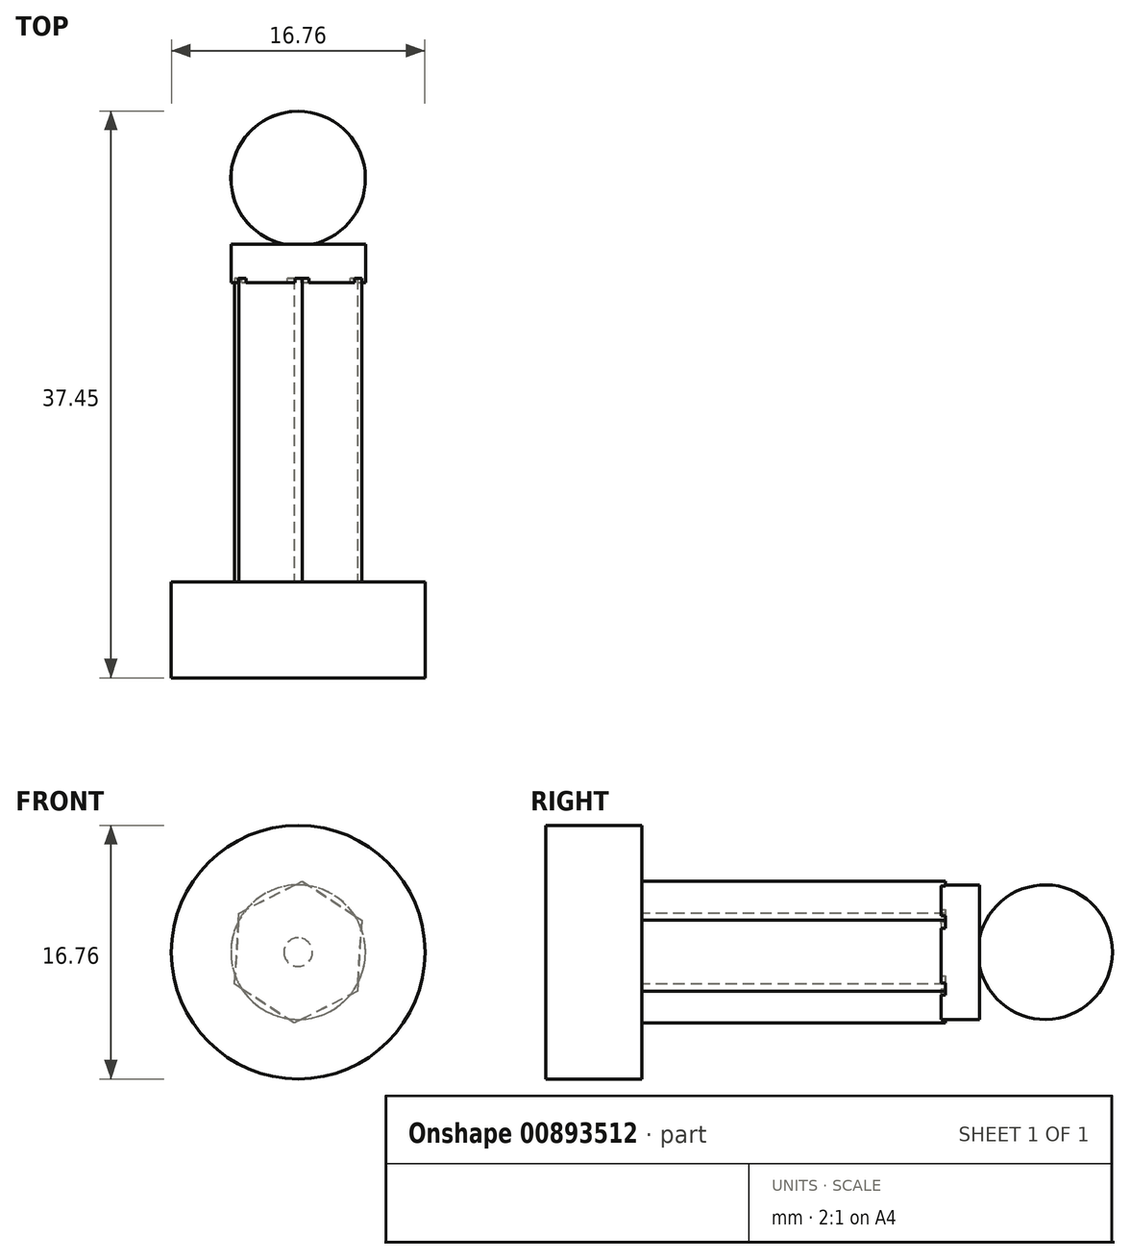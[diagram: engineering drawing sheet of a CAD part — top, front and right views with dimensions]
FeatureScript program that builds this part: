
annotation { "Feature Type Name" : "Feature", "Feature Type Description" : "" }
export const myFeature = defineFeature(function(context is Context, id is Id, definition is map)
    precondition{}
    {
        {
            var Q0;
            Q0=qCreatedBy(makeId("Top.planeOp"),FACE);
            var sketch = newSketch(context, id + "F0", { "sketchPlane" : qUnion([Q0])});
            skArc(sketch, "E0", {"start": v(0, 37.45) * mm, "mid": v(-4.42, 33.48) * mm, "end": v(-0.94, 28.66) * mm});
            skLineSegment(sketch, "E1", {"start": v(0, 37.45) * mm, "end": v(0, 28.56) * mm});
            skLineSegment(sketch, "E2", {"start": v(0, 37.45) * mm, "end": v(0, 28.56) * mm, "construction": true});
            skLineSegment(sketch, "E3", {"start": v(0, 28.56) * mm, "end": v(0, 26.02) * mm, "construction": true});
            skLineSegment(sketch, "E4.bottom", {"start": v(-0.94, 28.66) * mm, "end": v(-4.45, 28.66) * mm});
            skLineSegment(sketch, "E4.top", {"start": v(0, 26.12) * mm, "end": v(-4.45, 26.12) * mm});
            skLineSegment(sketch, "E4.left", {"start": v(0, 28.66) * mm, "end": v(0, 26.12) * mm});
            skLineSegment(sketch, "E4.right", {"start": v(-4.45, 28.66) * mm, "end": v(-4.45, 26.12) * mm});
            skSolve(sketch);
        }
        {
            var Q0;
            Q0=makeQuery(id+"F0.imprint","IMPRINT",FACE,{"disambiguationData":[TD([[makeQuery(id+"F0.imprint","IMPRINT",EDGE,{"derivedFrom":sQuery(id+"F0.wireOp",EDGE,"E0")}),1.0]])]});
            var Q1;
            Q1=sQuery(id+"F0.wireOp",EDGE,"E1");
            revolve(context, id + "F1", {"surfaceOperationType" : NewSurfaceOperationType.NEW, "entities" : qUnion([Q0]), "axis" : qUnion([Q1]), "revolveType" : RevolveType.FULL});
        }
        {
            var Q0;
            Q0=qCreatedBy(makeId("Front.planeOp"),FACE);
            var sketch = newSketch(context, id + "F2", { "sketchPlane" : qUnion([Q0])});
            skCircle(sketch, "E5", {"center": v(0, 0) * mm, "radius": 8.38 * mm});
            skCircle(sketch, "E6.cCircle", {"center": v(0, 0) * mm, "radius": 4.06 * mm, "construction": true});
            skLineSegment(sketch, "E6.0", {"start": v(-0.27, -4.68) * mm, "end": v(-4.2, -2.1) * mm});
            skLineSegment(sketch, "E6.1", {"start": v(-4.2, -2.1) * mm, "end": v(-3.92, 2.58) * mm});
            skLineSegment(sketch, "E6.2", {"start": v(-3.92, 2.58) * mm, "end": v(0.27, 4.68) * mm});
            skLineSegment(sketch, "E6.3", {"start": v(0.27, 4.68) * mm, "end": v(4.2, 2.1) * mm});
            skLineSegment(sketch, "E6.4", {"start": v(4.2, 2.1) * mm, "end": v(3.92, -2.58) * mm});
            skLineSegment(sketch, "E6.5", {"start": v(3.92, -2.58) * mm, "end": v(-0.27, -4.68) * mm});
            skPoint(sketch, "E6.0.midPoint", {"position": v(-2.23, -3.4) * mm});
            skSolve(sketch);
        }
        {
            var Q0;
            Q0=makeQuery(id+"F2.imprint","IMPRINT",FACE,{"disambiguationData":[TD([[makeQuery(id+"F2.imprint","IMPRINT",EDGE,{"derivedFrom":sQuery(id+"F2.wireOp",EDGE,"E6.0")}),-1.0]])]});
            extrude(context, id + "F3", {"entities" : qUnion([Q0]), "operationType" : NewBodyOperationType.ADD, "oppositeDirection" : true, "depth" : 26.42 * mm, "offsetDistance" : 25.4 * mm});
        }
        {
            var Q0;
            Q0=makeQuery(id+"F2.imprint","IMPRINT",FACE,{"disambiguationData":[TD([[makeQuery(id+"F2.imprint","IMPRINT",EDGE,{"derivedFrom":sQuery(id+"F2.wireOp",EDGE,"E5")}),1.0]])]});
            extrude(context, id + "F4", {"entities" : qUnion([Q0]), "operationType" : NewBodyOperationType.ADD, "oppositeDirection" : true, "depth" : 6.35 * mm, "offsetDistance" : 25.4 * mm});
        }
    });
